# Revit family: KSP-D_SIDE
name_source: partatom
category: Mechanical Equipment
units: mm (PartAtom-declared; Revit-internal decimal feet)

## family parameters
Always vertical = Yes
Cut with Voids When Loaded = No
Part Type = Normal
Room Calculation Point = No
Round Connector Dimension = Use Diameter
Shared = No
Work Plane-Based = No

## types (16) — shared parameters
0 = 0' - 0"
1.5 = 0' - 1 1/2"
2" = 0' - 2"
3/4 = 0' - 0 3/4"
4 = 0' - 4"
G = 0' - 3"
Manufacturer = Loren Cook Company
Model = KSP-D_Side
ONE EIGTH = 0' - 0 1/8"
OP_HEIGHT = 1' - 0 13/16"
Type Comments = Filtered Kitchen Supply Packaged Ventilator Direct Drive Side Discharge
URL = www.lorencook.com

## per-type parameters (varying)
| type | -(C_W/2) | A | A/2 | B | C_H | C_W | C_W/2 | D | E | F | FILTER_H | FILTER_W | H | K | RO | RO/2 | T_SQ | T_SQ/2 | W | W/2 |
| 94KSPD_Side | -0' - 9 5/8" | 2' - 0 3/16" | 1' - 0 3/32" | 2' - 0" | 1' - 6" | 1' - 7 1/4" | 0' - 9 5/8" | 1' - 5 1/4" | 0' - 9 13/16" | 0' - 10 5/8" | 1' - 10 3/4" | 1' - 5 3/4" | 0' - 3" | 0' - 6 1/4" | 1' - 7 1/2" | 0' - 9 3/4" | 2' - 0 1/8" | 1' - 0 1/16" | 0' - 4 9/16" | 0' - 2 9/32" |
| 103KSPD_Side | -0' - 11 1/8" | 2' - 4 3/16" | 1' - 2 3/32" | 2' - 3" | 1' - 9" | 1' - 10 1/4" | 0' - 11 1/8" | 1' - 8 1/4" | 0' - 9 13/16" | 1' - 0 3/16" | 2' - 3" | 1' - 9 3/4" | 0' - 3 7/8" | 0' - 6 1/4" | 1' - 11 1/2" | 0' - 11 3/4" | 2' - 4 1/8" | 1' - 2 1/16" | 0' - 8 9/16" | 0' - 4 9/32" |
| 122KSPD_Side | -1' - 1 1/4" | 2' - 8 3/16" | 1' - 4 3/32" | 2' - 8 1/4" | 2' - 2 3/16" | 2' - 2 1/2" | 1' - 1 1/4" | 2' - 1 5/8" | 0' - 6 7/8" | 1' - 1 11/16" | 2' - 10 3/8" | 2' - 1 3/4" | 0' - 4 7/8" | 0' - 3 7/16" | 2' - 3 1/2" | 1' - 1 3/4" | 2' - 8 1/8" | 1' - 4 1/16" | 1' - 6 7/8" | 0' - 9 7/16" |
| 96KSPD_Side | -0' - 9 5/8" | 2' - 0 3/16" | 1' - 0 3/32" | 2' - 0" | 1' - 6" | 1' - 7 1/4" | 0' - 9 5/8" | 1' - 5 1/4" | 0' - 9 5/8" | 0' - 10 7/16" | 1' - 10 3/4" | 1' - 5 3/4" | 0' - 3 7/16" | 0' - 6 1/4" | 1' - 7 1/2" | 0' - 9 3/4" | 2' - 0 1/8" | 1' - 0 1/16" | 0' - 4 7/8" | 0' - 2 7/16" |
| 98KSPD_Side | -0' - 9 5/8" | 2' - 0 3/16" | 1' - 0 3/32" | 2' - 0" | 1' - 6" | 1' - 7 1/4" | 0' - 9 5/8" | 1' - 5 1/4" | 0' - 9 1/4" | 0' - 10 1/4" | 1' - 10 3/4" | 1' - 5 3/4" | 0' - 3 7/8" | 0' - 6 1/4" | 1' - 7 1/2" | 0' - 9 3/4" | 2' - 0 1/8" | 1' - 0 1/16" | 0' - 5 5/8" | 0' - 2 13/16" |
| 125KSPD_Side | -1' - 1 1/4" | 2' - 8 3/16" | 1' - 4 3/32" | 2' - 8 1/4" | 2' - 2 3/16" | 2' - 2 1/2" | 1' - 1 1/4" | 2' - 1 5/8" | 0' - 4 7/8" | 1' - 2" | 2' - 10 3/8" | 2' - 1 3/4" | 0' - 4 7/8" | 0' - 3 15/16" | 2' - 3 1/2" | 1' - 1 3/4" | 2' - 8 1/8" | 1' - 4 1/16" | 1' - 10 1/2" | 0' - 11 1/4" |
| 95KSPD_Side | -0' - 9 5/8" | 2' - 0 3/16" | 1' - 0 3/32" | 2' - 0" | 1' - 6" | 1' - 7 1/4" | 0' - 9 5/8" | 1' - 5 1/4" | 0' - 9 13/16" | 0' - 10 5/8" | 1' - 10 3/4" | 1' - 5 3/4" | 0' - 3" | 0' - 6 1/4" | 1' - 7 1/2" | 0' - 9 3/4" | 2' - 0 1/8" | 1' - 0 1/16" | 0' - 4 9/16" | 0' - 2 9/32" |
| 97KSPD_Side | -0' - 9 5/8" | 2' - 0 3/16" | 1' - 0 3/32" | 2' - 0" | 1' - 6" | 1' - 7 1/4" | 0' - 9 5/8" | 1' - 5 1/4" | 0' - 9 5/8" | 0' - 10 7/16" | 1' - 10 3/4" | 1' - 5 3/4" | 0' - 3 7/16" | 0' - 6 1/4" | 1' - 7 1/2" | 0' - 9 3/4" | 2' - 0 1/8" | 1' - 0 1/16" | 0' - 4 7/8" | 0' - 2 7/16" |
| 99KSPD_Side | -0' - 9 5/8" | 2' - 0 3/16" | 1' - 0 3/32" | 2' - 0" | 1' - 6" | 1' - 7 1/4" | 0' - 9 5/8" | 1' - 5 1/4" | 0' - 9 1/4" | 0' - 10 1/4" | 1' - 10 3/4" | 1' - 5 3/4" | 0' - 3 7/8" | 0' - 6 1/4" | 1' - 7 1/2" | 0' - 9 3/4" | 2' - 0 1/8" | 1' - 0 1/16" | 0' - 5 5/8" | 0' - 2 13/16" |
| 104KSPD_Side | -0' - 11 1/8" | 2' - 4 3/16" | 1' - 2 3/32" | 2' - 3" | 1' - 9" | 1' - 10 1/4" | 0' - 11 1/8" | 1' - 8 1/4" | 0' - 9 13/16" | 1' - 0 3/16" | 2' - 3" | 1' - 9 3/4" | 0' - 3 7/8" | 0' - 6 1/4" | 1' - 11 1/2" | 0' - 11 3/4" | 2' - 4 1/8" | 1' - 2 1/16" | 0' - 8 9/16" | 0' - 4 9/32" |
| 105KSPD_Side | -0' - 11 1/8" | 2' - 4 3/16" | 1' - 2 3/32" | 2' - 3" | 1' - 9" | 1' - 10 1/4" | 0' - 11 1/8" | 1' - 8 1/4" | 0' - 9 13/16" | 1' - 0 3/16" | 2' - 3" | 1' - 9 3/4" | 0' - 3 7/8" | 0' - 6 1/4" | 1' - 11 1/2" | 0' - 11 3/4" | 2' - 4 1/8" | 1' - 2 1/16" | 0' - 8 9/16" | 0' - 4 9/32" |
| 106KSPD_Side | -0' - 11 1/8" | 2' - 4 3/16" | 1' - 2 3/32" | 2' - 3" | 1' - 9" | 1' - 10 1/4" | 0' - 11 1/8" | 1' - 8 1/4" | 0' - 9 13/16" | 1' - 0 3/16" | 2' - 3" | 1' - 9 3/4" | 0' - 3 7/8" | 0' - 6 1/4" | 1' - 11 1/2" | 0' - 11 3/4" | 2' - 4 1/8" | 1' - 2 1/16" | 0' - 8 9/16" | 0' - 4 9/32" |
| 123KSPD_Side | -1' - 1 1/4" | 2' - 8 3/16" | 1' - 4 3/32" | 2' - 8 1/4" | 2' - 2 3/16" | 2' - 2 1/2" | 1' - 1 1/4" | 2' - 1 5/8" | 0' - 6 7/8" | 1' - 1 11/16" | 2' - 10 3/8" | 2' - 1 3/4" | 0' - 4 7/8" | 0' - 3 7/16" | 2' - 3 1/2" | 1' - 1 3/4" | 2' - 8 1/8" | 1' - 4 1/16" | 1' - 6 7/8" | 0' - 9 7/16" |
| 124KSPD_Side | -1' - 1 1/4" | 2' - 8 3/16" | 1' - 4 3/32" | 2' - 8 1/4" | 2' - 2 3/16" | 2' - 2 1/2" | 1' - 1 1/4" | 2' - 1 5/8" | 0' - 6 7/8" | 1' - 1 11/16" | 2' - 10 3/8" | 2' - 1 3/4" | 0' - 4 7/8" | 0' - 3 7/16" | 2' - 3 1/2" | 1' - 1 3/4" | 2' - 8 1/8" | 1' - 4 1/16" | 1' - 6 7/8" | 0' - 9 7/16" |
| 126KSPD_Side | -1' - 1 1/4" | 2' - 8 3/16" | 1' - 4 3/32" | 2' - 8 1/4" | 2' - 2 3/16" | 2' - 2 1/2" | 1' - 1 1/4" | 2' - 1 5/8" | 0' - 4 7/8" | 1' - 2" | 2' - 10 3/8" | 2' - 1 3/4" | 0' - 4 7/8" | 0' - 3 15/16" | 2' - 3 1/2" | 1' - 1 3/4" | 2' - 8 1/8" | 1' - 4 1/16" | 1' - 10 1/2" | 0' - 11 1/4" |
| 127KSPD_Side | -1' - 1 1/4" | 2' - 8 3/16" | 1' - 4 3/32" | 2' - 8 1/4" | 2' - 2 3/16" | 2' - 2 1/2" | 1' - 1 1/4" | 2' - 1 5/8" | 0' - 4 7/8" | 1' - 2" | 2' - 10 3/8" | 2' - 1 3/4" | 0' - 4 7/8" | 0' - 3 15/16" | 2' - 3 1/2" | 1' - 1 3/4" | 2' - 8 1/8" | 1' - 4 1/16" | 1' - 10 1/2" | 0' - 11 1/4" |

## geometry (parser evidence)
native form markers: Sweep x2
no freeform markers — native parametric forms only
